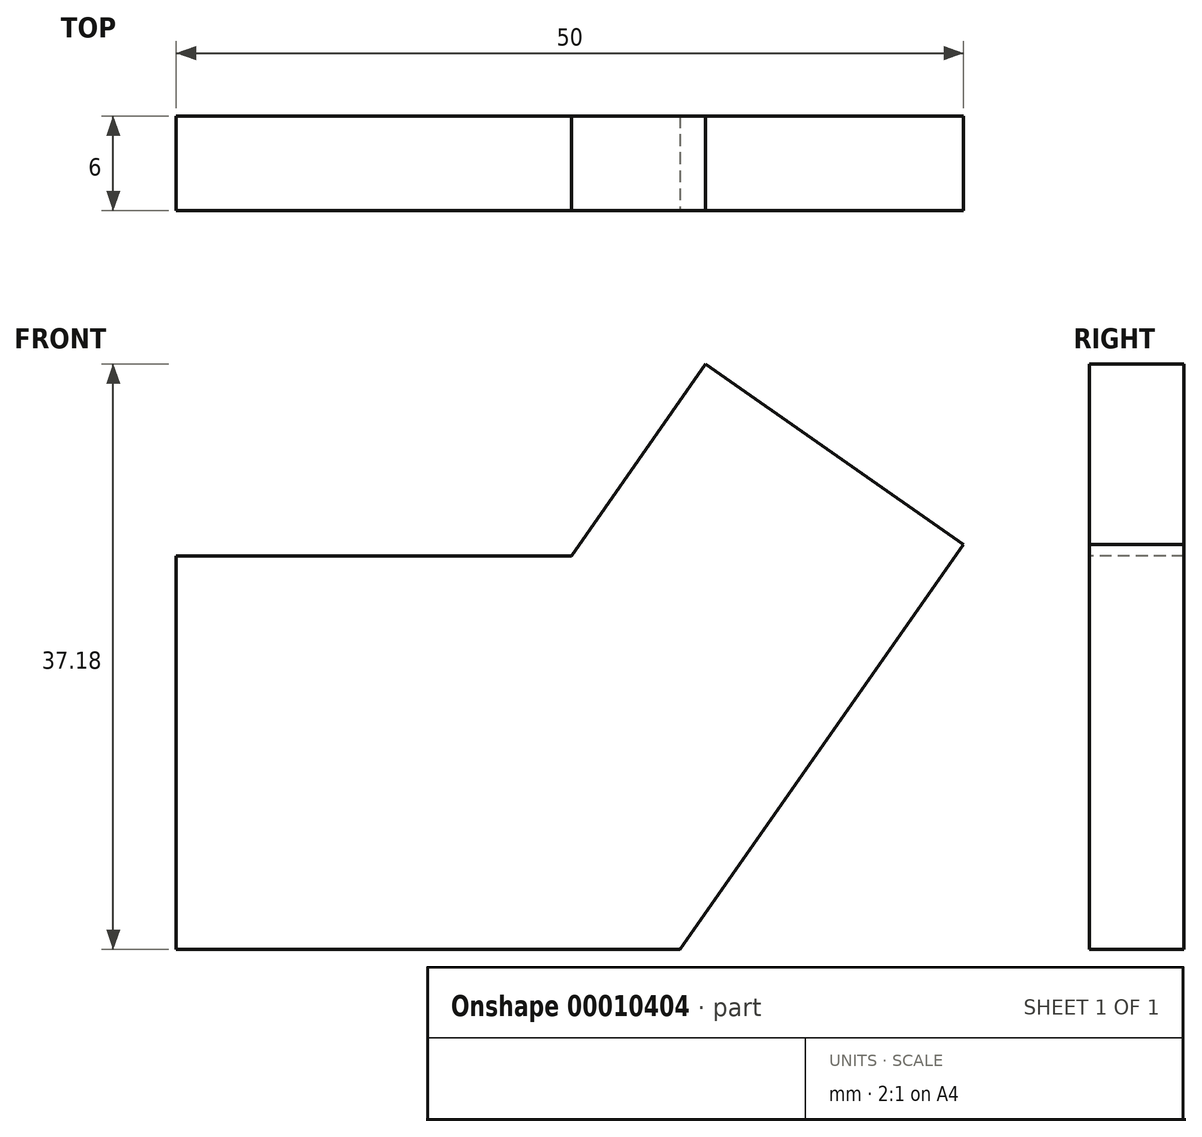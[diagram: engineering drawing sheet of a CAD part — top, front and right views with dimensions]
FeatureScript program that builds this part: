
annotation { "Feature Type Name" : "Feature", "Feature Type Description" : "" }
export const myFeature = defineFeature(function(context is Context, id is Id, definition is map)
    precondition{}
    {
        {
            var Q0;
            Q0=qCreatedBy(makeId("Front.planeOp"),FACE);
            var sketch = newSketch(context, id + "F0", { "sketchPlane" : qUnion([Q0])});
            skLineSegment(sketch, "E0", {"start": v(0, 0) * mm, "end": v(32, 0) * mm});
            skLineSegment(sketch, "E1", {"start": v(32, 0) * mm, "end": v(50, 25.7) * mm});
            skLineSegment(sketch, "E2", {"start": v(50, 25.7) * mm, "end": v(33.62, 37.18) * mm});
            skLineSegment(sketch, "E3", {"start": v(33.62, 37.18) * mm, "end": v(25.09, 25) * mm});
            skLineSegment(sketch, "E4", {"start": v(25.09, 25) * mm, "end": v(0, 25) * mm});
            skLineSegment(sketch, "E5", {"start": v(0, 25) * mm, "end": v(0, 0) * mm});
            skSolve(sketch);
        }
        {
            var Q0;
            Q0 = qSketchRegion(id + "F0", true);
            extrude(context, id + "F1", {"entities" : qUnion([Q0]), "oppositeDirection" : true, "depth" : 6 * mm});
        }
    });
